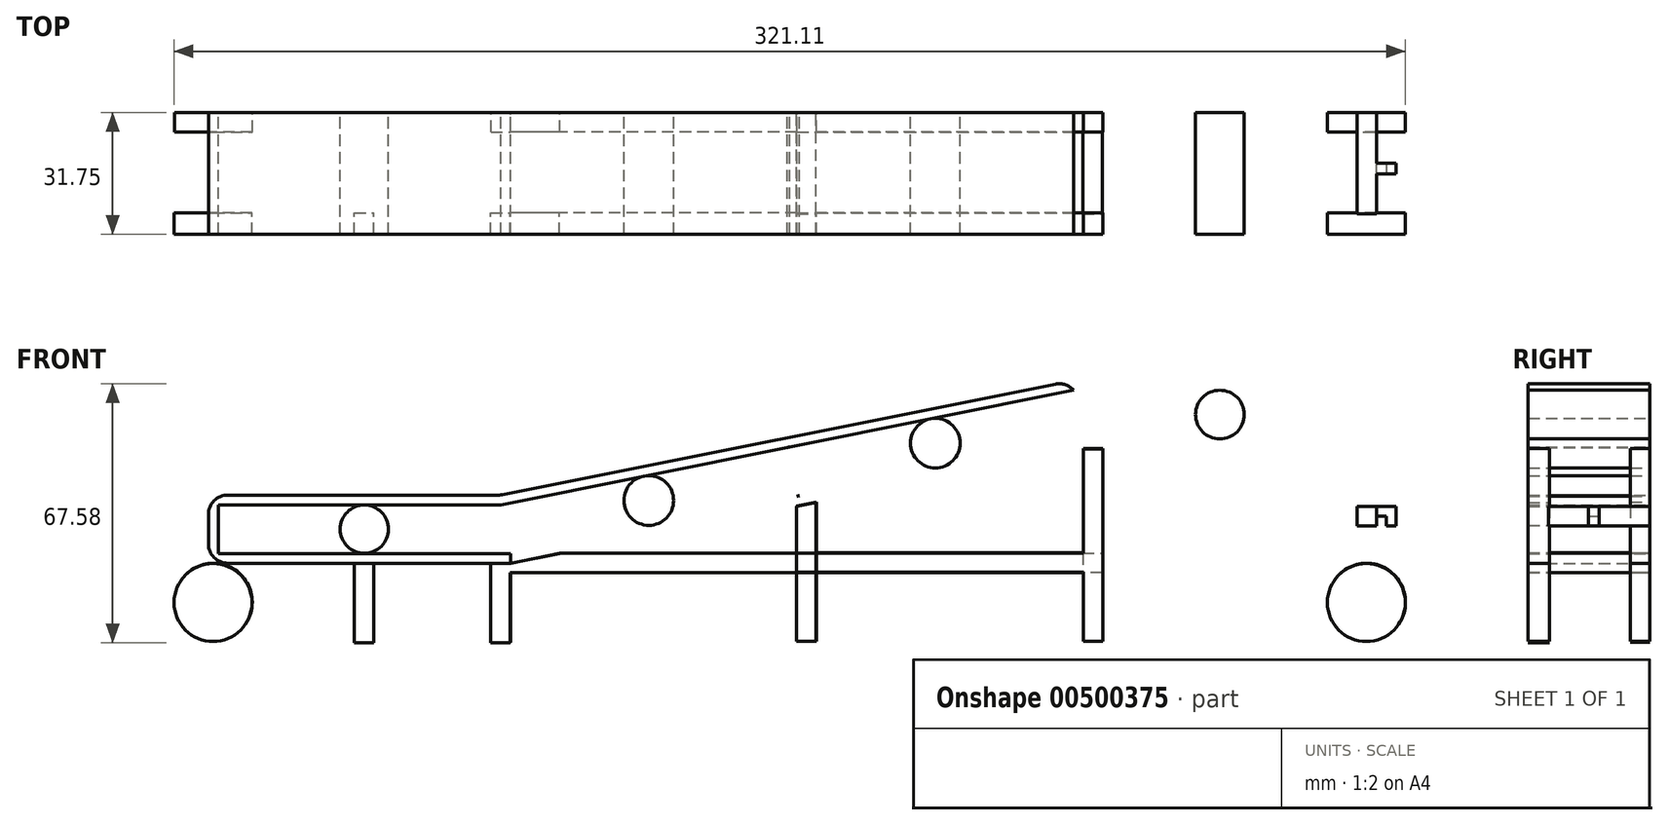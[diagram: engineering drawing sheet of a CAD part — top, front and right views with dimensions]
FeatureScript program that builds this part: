
annotation { "Feature Type Name" : "Feature", "Feature Type Description" : "" }
export const myFeature = defineFeature(function(context is Context, id is Id, definition is map)
    precondition{}
    {
        {
            var Q0;
            Q0=qCreatedBy(makeId("Front.planeOp"),FACE);
            var sketch = newSketch(context, id + "F0", { "sketchPlane" : qUnion([Q0])});
            skLineSegment(sketch, "E0", {"start": v(-75.53, -39.8) * mm, "end": v(73.9, -9.92) * mm});
            skLineSegment(sketch, "E1", {"start": v(73.9, -9.92) * mm, "end": v(76.45, -22.62) * mm});
            skLineSegment(sketch, "E2", {"start": v(76.45, -22.62) * mm, "end": v(-73, -52.5) * mm});
            skLineSegment(sketch, "E3", {"start": v(-73, -52.5) * mm, "end": v(-75.53, -39.8) * mm});
            skLineSegment(sketch, "E4", {"start": v(73.9, -9.92) * mm, "end": v(150.1, -9.92) * mm});
            skLineSegment(sketch, "E5", {"start": v(150.1, -9.92) * mm, "end": v(150.1, -22.62) * mm});
            skLineSegment(sketch, "E6", {"start": v(150.1, -22.62) * mm, "end": v(76.45, -22.62) * mm});
            skLineSegment(sketch, "E7", {"start": v(-75.53, -39.8) * mm, "end": v(-149.2, -39.8) * mm});
            skLineSegment(sketch, "E8", {"start": v(-149.2, -39.8) * mm, "end": v(-149.2, -52.5) * mm});
            skLineSegment(sketch, "E9", {"start": v(-149.2, -52.5) * mm, "end": v(-73, -52.5) * mm});
            skLineSegment(sketch, "E10", {"start": v(-149.2, -52.5) * mm, "end": v(-111.1, -52.5) * mm});
            skLineSegment(sketch, "E11", {"start": v(-73, -52.5) * mm, "end": v(1.73, -37.56) * mm});
            skLineSegment(sketch, "E12", {"start": v(1.73, -37.56) * mm, "end": v(-35.63, -45.03) * mm});
            skLineSegment(sketch, "E13", {"start": v(-0.81, -24.86) * mm, "end": v(36.55, -17.39) * mm});
            skLineSegment(sketch, "E14", {"start": v(73.9, -9.92) * mm, "end": v(112, -9.92) * mm});
            skLineSegment(sketch, "E15", {"start": v(-149.2, -55.04) * mm, "end": v(-73, -55.04) * mm});
            skLineSegment(sketch, "E16", {"start": v(76.45, -25.16) * mm, "end": v(152.65, -25.16) * mm});
            skLineSegment(sketch, "E17", {"start": v(150.1, -25.16) * mm, "end": v(152.65, -25.16) * mm});
            skLineSegment(sketch, "E18", {"start": v(-149.2, -55.04) * mm, "end": v(-151.73, -55.04) * mm});
            skLineSegment(sketch, "E19", {"start": v(-151.73, -55.04) * mm, "end": v(-151.73, -37.26) * mm});
            skLineSegment(sketch, "E20", {"start": v(-151.73, -37.26) * mm, "end": v(-75.53, -37.26) * mm});
            skLineSegment(sketch, "E21", {"start": v(-75.53, -37.26) * mm, "end": v(73.93, -7.37) * mm});
            skLineSegment(sketch, "E22", {"start": v(152.65, -25.16) * mm, "end": v(152.65, -7.38) * mm});
            skLineSegment(sketch, "E23", {"start": v(152.65, -7.38) * mm, "end": v(73.93, -7.38) * mm});
            skLineSegment(sketch, "E24", {"start": v(73.9, -9.92) * mm, "end": v(73.93, -7.37) * mm});
            skLineSegment(sketch, "E25", {"start": v(150.1, -22.62) * mm, "end": v(150.1, -25.16) * mm});
            skPoint(sketch, "E26", {"position": v(-74.26, -46.15) * mm});
            skCircle(sketch, "E27", {"center": v(-111.1, -46.15) * mm, "radius": 6.3 * mm});
            skCircle(sketch, "E28", {"center": v(0.78, -31.15) * mm, "radius": 6.48 * mm});
            skCircle(sketch, "E29", {"center": v(37.82, -23.74) * mm, "radius": 6.46 * mm});
            skCircle(sketch, "E30", {"center": v(112, -16.27) * mm, "radius": 6.35 * mm});
            skCircle(sketch, "E31", {"center": v(-36.9, -38.68) * mm, "radius": 6.48 * mm});
            skLineSegment(sketch, "E32", {"start": v(152.8, -55.04) * mm, "end": v(152.65, -25.16) * mm});
            skLineSegment(sketch, "E33", {"start": v(152.8, -55.04) * mm, "end": v(147.72, -55.04) * mm});
            skLineSegment(sketch, "E34", {"start": v(147.72, -55.04) * mm, "end": v(147.72, -25.16) * mm});
            skLineSegment(sketch, "E35", {"start": v(1.73, -40.1) * mm, "end": v(1.73, -55.04) * mm});
            skLineSegment(sketch, "E36", {"start": v(6.8, -54.87) * mm, "end": v(6.8, -39.08) * mm});
            skLineSegment(sketch, "E37", {"start": v(76.45, -25.16) * mm, "end": v(76.45, -54.87) * mm});
            skLineSegment(sketch, "E38", {"start": v(81.53, -55.04) * mm, "end": v(81.53, -25.16) * mm});
            skCircle(sketch, "E39", {"center": v(150.26, -65.2) * mm, "radius": 10.16 * mm});
            skLineSegment(sketch, "E40", {"start": v(150.26, -65.2) * mm, "end": v(150.26, -55.04) * mm});
            skLineSegment(sketch, "E41", {"start": v(1.73, -55.04) * mm, "end": v(1.73, -75.36) * mm});
            skLineSegment(sketch, "E42", {"start": v(6.8, -54.87) * mm, "end": v(6.8, -75.36) * mm});
            skLineSegment(sketch, "E43", {"start": v(76.45, -54.87) * mm, "end": v(76.45, -75.36) * mm});
            skLineSegment(sketch, "E44", {"start": v(81.53, -55.04) * mm, "end": v(81.53, -75.36) * mm});
            skLineSegment(sketch, "E45", {"start": v(1.73, -75.36) * mm, "end": v(6.8, -75.36) * mm});
            skLineSegment(sketch, "E46", {"start": v(76.45, -75.36) * mm, "end": v(81.53, -75.36) * mm});
            skLineSegment(sketch, "E47", {"start": v(-73, -55.04) * mm, "end": v(-73, -75.7) * mm});
            skLineSegment(sketch, "E48", {"start": v(-73, -75.7) * mm, "end": v(-78.07, -75.7) * mm});
            skLineSegment(sketch, "E49", {"start": v(-78.07, -75.7) * mm, "end": v(-78.07, -55.04) * mm});
            skPoint(sketch, "E50", {"position": v(-150.46, -55.04) * mm});
            skCircle(sketch, "E51", {"center": v(-150.46, -65.2) * mm, "radius": 10.16 * mm});
            skLineSegment(sketch, "E52", {"start": v(-150.46, -65.2) * mm, "end": v(-150.46, -55.04) * mm});
            skLineSegment(sketch, "E53", {"start": v(-111.1, -55.04) * mm, "end": v(-113.63, -55.04) * mm});
            skLineSegment(sketch, "E54", {"start": v(-111.1, -55.04) * mm, "end": v(-108.55, -55.04) * mm});
            skLineSegment(sketch, "E55", {"start": v(-113.63, -55.04) * mm, "end": v(-113.63, -75.7) * mm});
            skLineSegment(sketch, "E56", {"start": v(-108.55, -55.04) * mm, "end": v(-108.55, -75.7) * mm});
            skLineSegment(sketch, "E57", {"start": v(-113.63, -75.7) * mm, "end": v(-108.55, -75.7) * mm});
            skLineSegment(sketch, "E58", {"start": v(76.45, -52.33) * mm, "end": v(6.8, -52.33) * mm});
            skLineSegment(sketch, "E59", {"start": v(6.8, -54.87) * mm, "end": v(6.8, -57.41) * mm});
            skLineSegment(sketch, "E60", {"start": v(6.8, -57.41) * mm, "end": v(76.45, -57.41) * mm});
            skLineSegment(sketch, "E61", {"start": v(76.45, -57.41) * mm, "end": v(76.45, -54.87) * mm});
            skLineSegment(sketch, "E62", {"start": v(6.8, -57.41) * mm, "end": v(-73, -57.41) * mm});
            skPoint(sketch, "E63", {"position": v(-60.15, -52.48) * mm});
            skLineSegment(sketch, "E64", {"start": v(-60.15, -52.48) * mm, "end": v(76.45, -25.16) * mm});
            skLineSegment(sketch, "E65", {"start": v(-73, -55.04) * mm, "end": v(-73, -52.5) * mm});
            skLineSegment(sketch, "E66", {"start": v(-60.15, -52.48) * mm, "end": v(-73, -55.04) * mm});
            skLineSegment(sketch, "E67", {"start": v(6.8, -52.33) * mm, "end": v(-60.15, -52.48) * mm});
            skSolve(sketch);
        }
        {
            var Q0;
            Q0=makeQuery(id+"F0.imprint","IMPRINT",FACE,{"disambiguationData":[TD([[makeQuery(id+"F0.imprint","IMPRINT",EDGE,{"derivedFrom":sQuery(id+"F0.wireOp",EDGE,"E4")}),1.0]])]});
            var Q1;
            {var subQ9=sQuery(id+"F0.wireOp",EDGE,"E11");Q1=makeQuery(id+"F0.imprint","IMPRINT",FACE,{"disambiguationData":[TD([[makeQuery(id+"F0.imprint","IMPRINT",EDGE,{"derivedFrom":subQ9}),-1.0]])]});}
            var Q2;
            {var subQ27=sQuery(id+"F0.wireOp",EDGE,"E7");Q2=makeQuery(id+"F0.imprint","IMPRINT",FACE,{"disambiguationData":[TD([[makeQuery(id+"F0.imprint","IMPRINT",EDGE,{"derivedFrom":subQ27}),-1.0]])]});}
            extrude(context, id + "F1", {"entities" : qUnion([Q0, Q1, Q2]), "depth" : 31.75 * mm});
        }
        {
            var Q0;
            Q0=makeQuery(id+"F0.imprint","IMPRINT",FACE,{"disambiguationData":[TD([[makeQuery(id+"F0.imprint","IMPRINT",EDGE,{"derivedFrom":sQuery(id+"F0.wireOp",EDGE,"E27")}),1.0]])]});
            var Q1;
            Q1=makeQuery(id+"F0.imprint","IMPRINT",FACE,{"disambiguationData":[TD([[makeQuery(id+"F0.imprint","IMPRINT",EDGE,{"derivedFrom":sQuery(id+"F0.wireOp",EDGE,"E29")}),1.0]])]});
            var Q2;
            {var subQ0=sQuery(id+"F0.wireOp",EDGE,"E30");var subQ2=makeQuery(id+"F0.imprint","INTERSECT",VERTEX,{"derivedFrom":[sQuery(id+"F0.wireOp",EDGE,"E6"),subQ0]});Q2=makeQuery(id+"F0.imprint","IMPRINT",FACE,{"disambiguationData":[TD([[makeQuery(id+"F0.imprint","IMPRINT",EDGE,{"disambiguationData":[TD([[subQ2,1.0]])],"derivedFrom":subQ0}),1.0]])]});}
            var Q3;
            {var subQ0=sQuery(id+"F0.wireOp",EDGE,"E31");var subQ2=makeQuery(id+"F0.imprint","INTERSECT",VERTEX,{"derivedFrom":[sQuery(id+"F0.wireOp",EDGE,"E0"),subQ0]});Q3=makeQuery(id+"F0.imprint","IMPRINT",FACE,{"disambiguationData":[TD([[makeQuery(id+"F0.imprint","IMPRINT",EDGE,{"disambiguationData":[TD([[subQ2,-1.0]])],"derivedFrom":subQ0}),1.0]])]});}
            var Q4;
            {var subQ0=sQuery(id+"F0.wireOp",EDGE,"E28");var subQ1=sQuery(id+"F0.wireOp",EDGE,"E2");var subQ3=makeQuery(id+"F0.imprint","INTERSECT",VERTEX,{"derivedFrom":[subQ1,subQ0]});Q4=makeQuery(id+"F0.imprint","IMPRINT",FACE,{"disambiguationData":[TD([[makeQuery(id+"F0.imprint","IMPRINT",EDGE,{"disambiguationData":[TD([[subQ3,-1.0]])],"derivedFrom":subQ0}),1.0]])]});}
            extrude(context, id + "F2", {"entities" : qUnion([Q0, Q1, Q2, Q3, Q4]), "operationType" : NewBodyOperationType.ADD, "depth" : 31.75 * mm});
        }
        {
            var Q0;
            Q0=makeQuery(id+"F1.opExtrude","SWEPT_EDGE",EDGE,{"disambiguationData":[OSD([sQuery(id+"F0.wireOp",EDGE,"E19"),sQuery(id+"F0.wireOp",EDGE,"E20")])]});
            var Q1;
            Q1=makeQuery(id+"F1.opExtrude","SWEPT_EDGE",EDGE,{"disambiguationData":[OSD([sQuery(id+"F0.wireOp",EDGE,"E22"),sQuery(id+"F0.wireOp",EDGE,"E23")])]});
            var Q2;
            Q2=makeQuery(id+"F1.opExtrude","SWEPT_EDGE",EDGE,{"disambiguationData":[OSD([sQuery(id+"F0.wireOp",EDGE,"E18"),sQuery(id+"F0.wireOp",EDGE,"E19")])]});
            var Q3;
            Q3=makeQuery(id+"F1.opExtrude","SWEPT_EDGE",EDGE,{"disambiguationData":[OSD([sQuery(id+"F0.wireOp",EDGE,"E17"),sQuery(id+"F0.wireOp",EDGE,"E22")])]});
            var Q4;
            Q4=makeQuery(id+"F1.opExtrude","SWEPT_EDGE",EDGE,{"disambiguationData":[OSD([sQuery(id+"F0.wireOp",EDGE,"E21"),sQuery(id+"F0.wireOp",EDGE,"E24")])]});
            var Q5;
            Q5=makeQuery(id+"F1.opExtrude","SWEPT_EDGE",EDGE,{"disambiguationData":[OSD([sQuery(id+"F0.wireOp",EDGE,"E20"),sQuery(id+"F0.wireOp",EDGE,"E21")])]});
            fillet(context, id + "F3", {"entities" : qUnion([Q0, Q1, Q2, Q3, Q4, Q5]), "radius" : 5.08 * mm, "tangentPropagation" : true, "allowEdgeOverflow" : false});
        }
        {
            var Q0;
            {var subQ3=sQuery(id+"F0.wireOp",EDGE,"E17");Q0=makeQuery(id+"F0.imprint","IMPRINT",FACE,{"disambiguationData":[TD([[makeQuery(id+"F0.imprint","IMPRINT",EDGE,{"derivedFrom":subQ3}),-1.0]])]});}
            var Q1;
            Q1=makeQuery(id+"F0.imprint","IMPRINT",FACE,{"disambiguationData":[TD([[makeQuery(id+"F0.imprint","IMPRINT",EDGE,{"derivedFrom":sQuery(id+"F0.wireOp",EDGE,"E39")}),1.0]])]});
            var Q2;
            {var subQ0=sQuery(id+"F0.wireOp",EDGE,"E38");Q2=makeQuery(id+"F0.imprint","IMPRINT",FACE,{"disambiguationData":[TD([[makeQuery(id+"F0.imprint","IMPRINT",EDGE,{"derivedFrom":subQ0}),1.0]])]});}
            var Q3;
            {var subQ2=sQuery(id+"F0.wireOp",EDGE,"E58");Q3=makeQuery(id+"F0.imprint","IMPRINT",FACE,{"disambiguationData":[TD([[makeQuery(id+"F0.imprint","IMPRINT",EDGE,{"derivedFrom":subQ2}),1.0]])]});}
            var Q4;
            {var subQ4=sQuery(id+"F0.wireOp",EDGE,"E35");Q4=makeQuery(id+"F0.imprint","IMPRINT",FACE,{"disambiguationData":[TD([[makeQuery(id+"F0.imprint","IMPRINT",EDGE,{"derivedFrom":subQ4}),1.0]])]});}
            var Q5;
            {var subQ0=sQuery(id+"F0.wireOp",EDGE,"E47");Q5=makeQuery(id+"F0.imprint","IMPRINT",FACE,{"disambiguationData":[TD([[makeQuery(id+"F0.imprint","IMPRINT",EDGE,{"derivedFrom":subQ0}),-1.0]])]});}
            var Q6;
            Q6=makeQuery(id+"F0.imprint","IMPRINT",FACE,{"disambiguationData":[TD([[makeQuery(id+"F0.imprint","IMPRINT",EDGE,{"derivedFrom":sQuery(id+"F0.wireOp",EDGE,"E53")}),1.0]])]});
            var Q7;
            Q7=makeQuery(id+"F0.imprint","IMPRINT",FACE,{"disambiguationData":[TD([[makeQuery(id+"F0.imprint","IMPRINT",EDGE,{"derivedFrom":sQuery(id+"F0.wireOp",EDGE,"E51")}),1.0]])]});
            var Q8;
            {var subQ5=sQuery(id+"F0.wireOp",EDGE,"E41");var subQ6=sQuery(id+"F0.wireOp",EDGE,"E35");var subQ7=makeQuery(id+"F0.imprint","INTERSECT",VERTEX,{"derivedFrom":[subQ6,subQ5]});Q8=makeQuery(id+"F0.imprint","IMPRINT",FACE,{"disambiguationData":[TD([[makeQuery(id+"F0.imprint","IMPRINT",EDGE,{"disambiguationData":[TD([[subQ7,1.0]])],"derivedFrom":subQ6}),-1.0]])]});}
            var Q9;
            {var subQ4=sQuery(id+"F0.wireOp",EDGE,"E42");Q9=makeQuery(id+"F0.imprint","IMPRINT",FACE,{"disambiguationData":[TD([[makeQuery(id+"F0.imprint","IMPRINT",EDGE,{"derivedFrom":subQ4}),-1.0]])]});}
            var Q10;
            {var subQ5=sQuery(id+"F0.wireOp",EDGE,"E59");Q10=makeQuery(id+"F0.imprint","IMPRINT",FACE,{"disambiguationData":[TD([[makeQuery(id+"F0.imprint","IMPRINT",EDGE,{"derivedFrom":subQ5}),-1.0]])]});}
            extrude(context, id + "F4", {"entities" : qUnion([Q0, Q1, Q2, Q3, Q4, Q5, Q6, Q7, Q8, Q9, Q10]), "operationType" : NewBodyOperationType.ADD, "depth" : 5.08 * mm});
        }
        {
            var Q0;
            Q0=qCreatedBy(makeId("Front.planeOp"),FACE);
            var sketch = newSketch(context, id + "F5", { "sketchPlane" : qUnion([Q0])});
            skLineSegment(sketch, "E68", {"start": v(76.27, -52.45) * mm, "end": v(81.35, -52.45) * mm});
            skLineSegment(sketch, "E69", {"start": v(81.35, -52.45) * mm, "end": v(81.35, -57.53) * mm});
            skLineSegment(sketch, "E70", {"start": v(81.35, -57.53) * mm, "end": v(76.27, -57.51) * mm});
            skLineSegment(sketch, "E71", {"start": v(76.27, -52.45) * mm, "end": v(76.27, -57.51) * mm});
            skLineSegment(sketch, "E72", {"start": v(1.67, -52.3) * mm, "end": v(6.75, -52.3) * mm});
            skLineSegment(sketch, "E73", {"start": v(6.75, -52.3) * mm, "end": v(6.75, -57.39) * mm});
            skLineSegment(sketch, "E74", {"start": v(6.75, -57.39) * mm, "end": v(1.67, -57.37) * mm});
            skLineSegment(sketch, "E75", {"start": v(1.67, -52.3) * mm, "end": v(1.67, -57.37) * mm});
            skLineSegment(sketch, "E76", {"start": v(147.74, -40.27) * mm, "end": v(152.82, -40.27) * mm});
            skLineSegment(sketch, "E77", {"start": v(152.82, -40.27) * mm, "end": v(152.82, -45.35) * mm});
            skLineSegment(sketch, "E78", {"start": v(152.82, -45.35) * mm, "end": v(147.74, -45.34) * mm});
            skLineSegment(sketch, "E79", {"start": v(147.74, -40.27) * mm, "end": v(147.74, -45.34) * mm});
            skSolve(sketch);
        }
        {
            var Q0;
            Q0 = qSketchRegion(id + "F5", true);
            extrude(context, id + "F6", {"entities" : qUnion([Q0]), "depth" : 26.42 * mm});
        }
        {
            var Q0;
            Q0=qCreatedBy(makeId("Front.planeOp"),FACE);
            var sketch = newSketch(context, id + "F7", { "sketchPlane" : qUnion([Q0])});
            skLineSegment(sketch, "E80", {"start": v(-149.26, -55.14) * mm, "end": v(-73.06, -55.14) * mm});
            skLineSegment(sketch, "E81", {"start": v(76.38, -25.26) * mm, "end": v(152.58, -25.26) * mm});
            skLineSegment(sketch, "E82", {"start": v(152.73, -55.14) * mm, "end": v(152.58, -25.26) * mm});
            skLineSegment(sketch, "E83", {"start": v(147.65, -55.14) * mm, "end": v(147.65, -25.26) * mm});
            skLineSegment(sketch, "E84", {"start": v(1.66, -40.2) * mm, "end": v(1.66, -55.14) * mm});
            skLineSegment(sketch, "E85", {"start": v(6.74, -54.97) * mm, "end": v(6.74, -39.18) * mm});
            skLineSegment(sketch, "E86", {"start": v(76.38, -25.26) * mm, "end": v(76.38, -54.97) * mm});
            skLineSegment(sketch, "E87", {"start": v(81.46, -55.14) * mm, "end": v(81.46, -25.26) * mm});
            skCircle(sketch, "E88", {"center": v(150.2, -65.3) * mm, "radius": 10.16 * mm});
            skLineSegment(sketch, "E89", {"start": v(1.66, -55.14) * mm, "end": v(1.66, -75.46) * mm});
            skLineSegment(sketch, "E90", {"start": v(6.74, -54.97) * mm, "end": v(6.74, -75.46) * mm});
            skLineSegment(sketch, "E91", {"start": v(76.38, -54.97) * mm, "end": v(76.38, -75.46) * mm});
            skLineSegment(sketch, "E92", {"start": v(81.46, -55.14) * mm, "end": v(81.46, -75.46) * mm});
            skLineSegment(sketch, "E93", {"start": v(1.66, -75.46) * mm, "end": v(6.74, -75.46) * mm});
            skLineSegment(sketch, "E94", {"start": v(76.38, -75.46) * mm, "end": v(81.46, -75.46) * mm});
            skLineSegment(sketch, "E95", {"start": v(-73.06, -55.14) * mm, "end": v(-73.06, -75.8) * mm});
            skLineSegment(sketch, "E96", {"start": v(-73.06, -75.8) * mm, "end": v(-78.14, -75.8) * mm});
            skLineSegment(sketch, "E97", {"start": v(-78.14, -75.8) * mm, "end": v(-78.14, -55.14) * mm});
            skCircle(sketch, "E98", {"center": v(-150.53, -65.3) * mm, "radius": 10.16 * mm});
            skLineSegment(sketch, "E99", {"start": v(-113.7, -55.14) * mm, "end": v(-113.7, -75.8) * mm});
            skLineSegment(sketch, "E100", {"start": v(-108.62, -55.14) * mm, "end": v(-108.62, -75.8) * mm});
            skLineSegment(sketch, "E101", {"start": v(-113.7, -75.8) * mm, "end": v(-108.62, -75.8) * mm});
            skLineSegment(sketch, "E102", {"start": v(76.38, -52.43) * mm, "end": v(6.74, -52.43) * mm});
            skLineSegment(sketch, "E103", {"start": v(6.74, -57.51) * mm, "end": v(76.38, -57.51) * mm});
            skLineSegment(sketch, "E104", {"start": v(6.74, -57.51) * mm, "end": v(-73.06, -57.51) * mm});
            skLineSegment(sketch, "E105", {"start": v(-60.22, -52.58) * mm, "end": v(76.38, -25.26) * mm});
            skLineSegment(sketch, "E106", {"start": v(-60.22, -52.58) * mm, "end": v(-73.06, -55.14) * mm});
            skLineSegment(sketch, "E107", {"start": v(6.74, -52.43) * mm, "end": v(-60.22, -52.58) * mm});
            skSolve(sketch);
        }
        {
            var Q0;
            Q0=makeQuery(id+"F7.imprint","IMPRINT",FACE,{"disambiguationData":[TD([[makeQuery(id+"F7.imprint","IMPRINT",EDGE,{"derivedFrom":sQuery(id+"F7.wireOp",EDGE,"E88")}),1.0]])]});
            var Q1;
            {var subQ7=sQuery(id+"F7.wireOp",EDGE,"E102");Q1=makeQuery(id+"F7.imprint","IMPRINT",FACE,{"disambiguationData":[TD([[makeQuery(id+"F7.imprint","IMPRINT",EDGE,{"derivedFrom":subQ7}),1.0]])]});}
            var Q2;
            {var subQ0=sQuery(id+"F7.wireOp",EDGE,"E106");Q2=makeQuery(id+"F7.imprint","IMPRINT",FACE,{"disambiguationData":[TD([[makeQuery(id+"F7.imprint","IMPRINT",EDGE,{"derivedFrom":subQ0}),1.0]])]});}
            var Q3;
            {var subQ0=sQuery(id+"F7.wireOp",EDGE,"E105");var subQ1=sQuery(id+"F7.wireOp",EDGE,"E84");var subQ2=makeQuery(id+"F7.imprint","INTERSECT",VERTEX,{"derivedFrom":[subQ1,subQ0]});Q3=makeQuery(id+"F7.imprint","IMPRINT",FACE,{"disambiguationData":[TD([[makeQuery(id+"F7.imprint","IMPRINT",EDGE,{"disambiguationData":[TD([[subQ2,-1.0]])],"derivedFrom":subQ1}),1.0]])]});}
            var Q4;
            {var subQ0=sQuery(id+"F7.wireOp",EDGE,"E93");Q4=makeQuery(id+"F7.imprint","IMPRINT",FACE,{"disambiguationData":[TD([[makeQuery(id+"F7.imprint","IMPRINT",EDGE,{"derivedFrom":subQ0}),1.0]])]});}
            var Q5;
            {var subQ0=sQuery(id+"F7.wireOp",EDGE,"E96");Q5=makeQuery(id+"F7.imprint","IMPRINT",FACE,{"disambiguationData":[TD([[makeQuery(id+"F7.imprint","IMPRINT",EDGE,{"derivedFrom":subQ0}),-1.0]])]});}
            var Q6;
            {var subQ0=sQuery(id+"F7.wireOp",EDGE,"E99");Q6=makeQuery(id+"F7.imprint","IMPRINT",FACE,{"disambiguationData":[TD([[makeQuery(id+"F7.imprint","IMPRINT",EDGE,{"derivedFrom":subQ0}),1.0]])]});}
            var Q7;
            Q7=makeQuery(id+"F7.imprint","IMPRINT",FACE,{"disambiguationData":[TD([[makeQuery(id+"F7.imprint","IMPRINT",EDGE,{"derivedFrom":sQuery(id+"F7.wireOp",EDGE,"E98")}),1.0]])]});
            var Q8;
            Q8=makeQuery(id+"F4.opExtrude","CAP_FACE",FACE,{"disambiguationData":[OSD([sQuery(id+"F0.wireOp",EDGE,"E16"),sQuery(id+"F0.wireOp",EDGE,"E17"),sQuery(id+"F0.wireOp",EDGE,"E32"),sQuery(id+"F0.wireOp",EDGE,"E33"),sQuery(id+"F0.wireOp",EDGE,"E34")])],"isStart":true});
            var Q9;
            {var subQ0=sQuery(id+"F7.wireOp",EDGE,"E87");Q9=makeQuery(id+"F7.imprint","IMPRINT",FACE,{"disambiguationData":[TD([[makeQuery(id+"F7.imprint","IMPRINT",EDGE,{"derivedFrom":subQ0}),1.0]])]});}
            extrude(context, id + "F8", {"entities" : qUnion([Q0, Q1, Q2, Q3, Q4, Q5, Q6, Q7, Q8, Q9]), "depth" : 31.75 * mm, "hasSecondDirection" : true, "secondDirectionOppositeDirection" : false, "secondDirectionDepth" : 26.16 * mm});
        }
        {
            var Q0;
            Q0=makeQuery(id+"F6.opExtrude","SWEPT_FACE",FACE,{"disambiguationData":[OSD([sQuery(id+"F5.wireOp",EDGE,"E77")])]});
            var sketch = newSketch(context, id + "F9", { "sketchPlane" : qUnion([Q0])});
            skLineSegment(sketch, "E108", {"start": v(-13.2, -40.27) * mm, "end": v(-16.01, -40.27) * mm});
            skLineSegment(sketch, "E109", {"start": v(-16.01, -42.81) * mm, "end": v(-13.2, -42.81) * mm});
            skLineSegment(sketch, "E110", {"start": v(-16.01, -40.27) * mm, "end": v(-16.01, -42.81) * mm});
            skLineSegment(sketch, "E111", {"start": v(-13.2, -40.27) * mm, "end": v(-13.2, -42.81) * mm});
            skSolve(sketch);
        }
        {
            var Q0;
            Q0=makeQuery(id+"F9.imprint","IMPRINT",FACE,{"disambiguationData":[TD([[makeQuery(id+"F9.imprint","IMPRINT",EDGE,{"derivedFrom":sQuery(id+"F9.wireOp",EDGE,"E108")}),-1.0]])]});
            extrude(context, id + "F10", {"entities" : qUnion([Q0]), "operationType" : NewBodyOperationType.ADD, "depth" : 5.08 * mm});
        }
        {
            var Q0;
            Q0=makeQuery(id+"F10.boolean.opBoolean","MERGE",FACE,{"derivedFrom":[makeQuery(id+"F6.opExtrude","SWEPT_FACE",FACE,{"disambiguationData":[OSD([sQuery(id+"F5.wireOp",EDGE,"E76")])]}),makeQuery(id+"F10.opExtrude","SWEPT_FACE",FACE,{"disambiguationData":[OSD([sQuery(id+"F9.wireOp",EDGE,"E108")])]})]});
            var sketch = newSketch(context, id + "F11", { "sketchPlane" : qUnion([Q0])});
            skLineSegment(sketch, "E112", {"start": v(157.9, -13.2) * mm, "end": v(155.36, -13.2) * mm});
            skLineSegment(sketch, "E113", {"start": v(155.36, -13.2) * mm, "end": v(155.36, -16.01) * mm});
            skLineSegment(sketch, "E114", {"start": v(155.36, -16.01) * mm, "end": v(157.9, -16.01) * mm});
            skLineSegment(sketch, "E115", {"start": v(157.9, -16.01) * mm, "end": v(157.9, -13.2) * mm});
            skSolve(sketch);
        }
        {
            var Q0;
            Q0=makeQuery(id+"F11.imprint","IMPRINT",FACE,{"disambiguationData":[TD([[makeQuery(id+"F11.imprint","IMPRINT",EDGE,{"derivedFrom":sQuery(id+"F11.wireOp",EDGE,"E112")}),1.0]])]});
            extrude(context, id + "F12", {"entities" : qUnion([Q0]), "operationType" : NewBodyOperationType.ADD, "oppositeDirection" : true, "depth" : 5.08 * mm});
        }
    });
